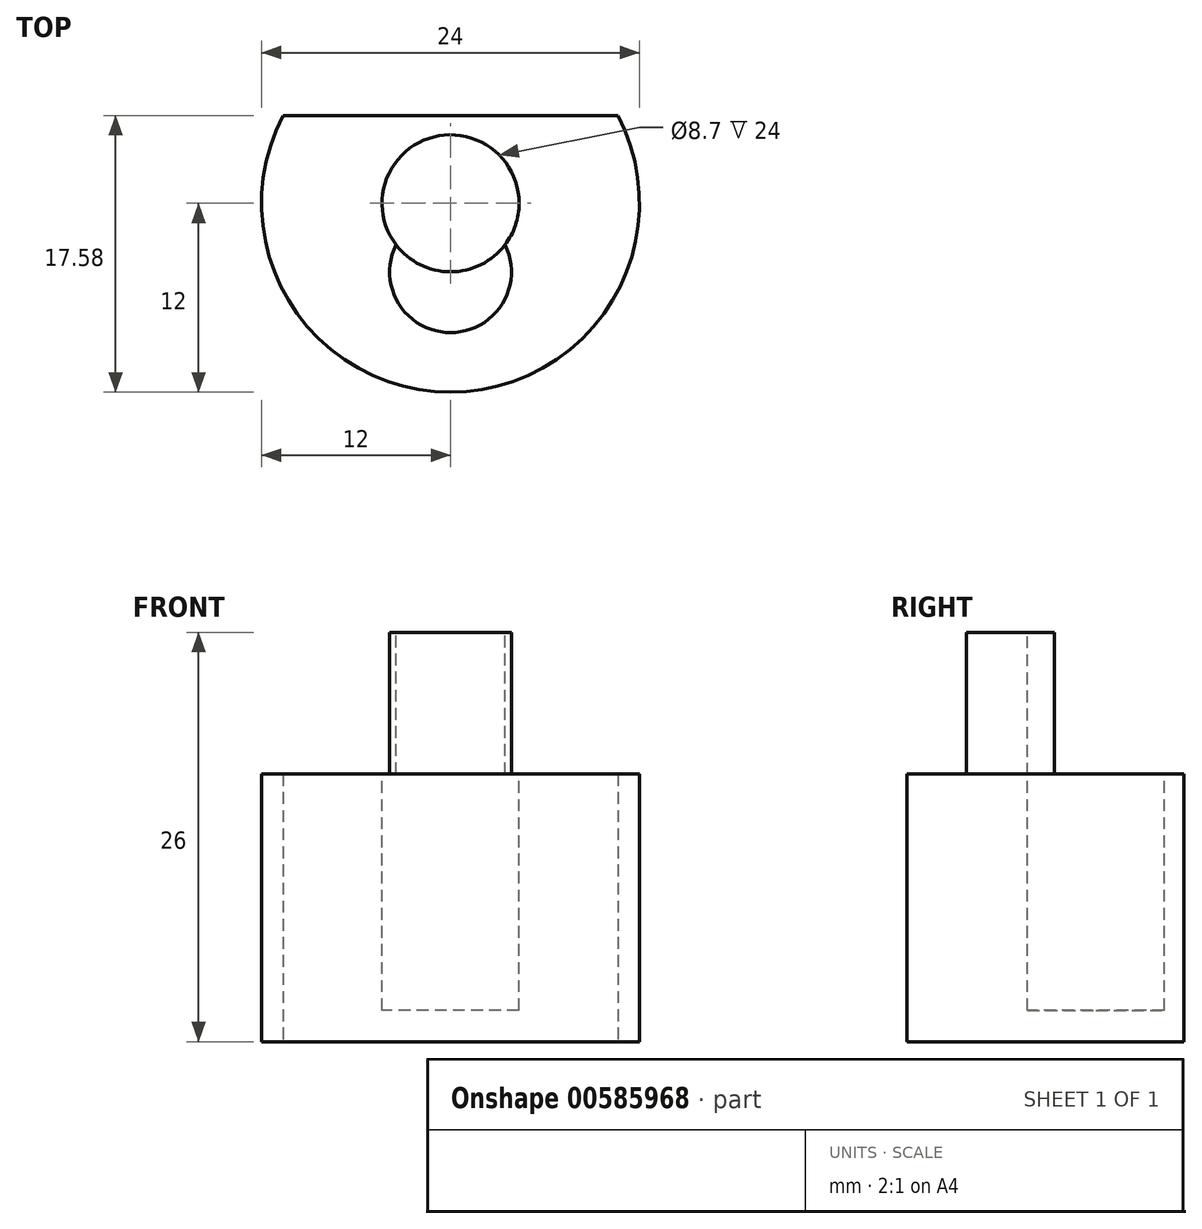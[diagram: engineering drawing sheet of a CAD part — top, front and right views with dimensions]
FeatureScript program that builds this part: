
annotation { "Feature Type Name" : "Feature", "Feature Type Description" : "" }
export const myFeature = defineFeature(function(context is Context, id is Id, definition is map)
    precondition{}
    {
        {
            var Q0;
            Q0=qCreatedBy(makeId("Top.planeOp"),FACE);
            var sketch = newSketch(context, id + "F0", { "sketchPlane" : qUnion([Q0])});
            skCircle(sketch, "E0", {"center": v(0, 0) * mm, "radius": 12 * mm});
            skSolve(sketch);
        }
        {
            var Q0;
            Q0 = qSketchRegion(id + "F0", true);
            extrude(context, id + "F1", {"entities" : qUnion([Q0]), "depth" : 26 * mm, "offsetDistance" : 25 * mm});
        }
        {
            var Q0;
            Q0=makeQuery(id+"F1.opExtrude","CAP_FACE",FACE,{"disambiguationData":[OSD([sQuery(id+"F0.wireOp",EDGE,"E0")])],"isStart":false});
            var sketch = newSketch(context, id + "F2", { "sketchPlane" : qUnion([Q0])});
            skCircle(sketch, "E1", {"center": v(0, 0) * mm, "radius": 4.35 * mm});
            skArc(sketch, "E2", {"start": v(-3.46, -2.63) * mm, "mid": v(0, -8.21) * mm, "end": v(3.46, -2.63) * mm});
            skSolve(sketch);
        }
        {
            var Q0;
            {var subQ0=sQuery(id+"F2.wireOp",EDGE,"E2");Q0=makeQuery(id+"F2.imprint","IMPRINT",FACE,{"disambiguationData":[TD([[makeQuery(id+"F2.imprint","IMPRINT",EDGE,{"derivedFrom":subQ0}),-1.0]])]});}
            var Q1;
            {var subQ0=sQuery(id+"F2.wireOp",EDGE,"E2");var subQ1=sQuery(id+"F2.wireOp",EDGE,"E1");var subQ2=makeQuery(id+"F2.imprint","INTERSECT",VERTEX,{"disambiguationData":[OD(0.0)],"derivedFrom":[subQ1,subQ0]});Q1=makeQuery(id+"F2.imprint","IMPRINT",FACE,{"disambiguationData":[TD([[makeQuery(id+"F2.imprint","IMPRINT",EDGE,{"disambiguationData":[TD([[subQ2,-1.0]])],"derivedFrom":subQ1}),1.0]])]});}
            extrude(context, id + "F3", {"entities" : qUnion([Q0, Q1]), "operationType" : NewBodyOperationType.REMOVE, "oppositeDirection" : true, "depth" : 9 * mm, "offsetDistance" : 25 * mm});
        }
        {
            var Q0;
            Q0=makeQuery(id+"F3.boolean.opBoolean","COPY",FACE,{"derivedFrom":makeQuery(id+"F3.opExtrude","CAP_FACE",FACE,{"disambiguationData":[OSD([sQuery(id+"F0.wireOp",EDGE,"E0"),sQuery(id+"F2.wireOp",EDGE,"E1"),sQuery(id+"F2.wireOp",EDGE,"E2")])],"isStart":false})});
            var sketch = newSketch(context, id + "F4", { "sketchPlane" : qUnion([Q0])});
            skCircle(sketch, "E3", {"center": v(0, 0) * mm, "radius": 4.35 * mm});
            skSolve(sketch);
        }
        {
            var Q0;
            {var subQ0=sQuery(id+"F4.wireOp",EDGE,"E3");var subQ1=makeQuery(id+"F3.boolean.opBoolean","COPY",EDGE,{"derivedFrom":makeQuery(id+"F3.opExtrude","CAP_EDGE",EDGE,{"disambiguationData":[OSD([sQuery(id+"F2.wireOp",EDGE,"E2")])],"isStart":false})});var subQ2=makeQuery(id+"F4.imprint","INTERSECT",VERTEX,{"disambiguationData":[OD(0.0)],"derivedFrom":[subQ1,subQ0]});Q0=makeQuery(id+"F4.imprint","IMPRINT",FACE,{"disambiguationData":[TD([[makeQuery(id+"F4.imprint","IMPRINT",EDGE,{"disambiguationData":[TD([[subQ2,-1.0]])],"derivedFrom":subQ0}),1.0]])]});}
            extrude(context, id + "F5", {"entities" : qUnion([Q0]), "operationType" : NewBodyOperationType.REMOVE, "oppositeDirection" : true, "depth" : 15 * mm, "offsetDistance" : 25 * mm});
        }
        {
            var Q0;
            Q0=qCreatedBy(makeId("Front.planeOp"),FACE);
            cPlane(context, id + "F6", {"entities" : qUnion([Q0]), "cplaneType" : CPlaneType.OFFSET, "offset" : 12 * mm, "oppositeDirection" : true, "width" : 150 * mm, "height" : 150 * mm});
        }
        {
            var Q0;
            Q0=qCreatedBy(id+"F6.planeOp",FACE);
            var sketch = newSketch(context, id + "F7", { "sketchPlane" : qUnion([Q0])});
            skLineSegment(sketch, "E4.bottom", {"start": v(0, 0) * mm, "end": v(-12, 0) * mm});
            skLineSegment(sketch, "E4.top", {"start": v(0, 17) * mm, "end": v(-12, 17) * mm});
            skLineSegment(sketch, "E4.left", {"start": v(0, 0) * mm, "end": v(0, 17) * mm});
            skLineSegment(sketch, "E4.right", {"start": v(-12, 0) * mm, "end": v(-12, 17) * mm});
            skLineSegment(sketch, "E5.bottom", {"start": v(0, 0) * mm, "end": v(12, 0) * mm});
            skLineSegment(sketch, "E5.top", {"start": v(0, 17) * mm, "end": v(12, 17) * mm});
            skLineSegment(sketch, "E5.right", {"start": v(12, 0) * mm, "end": v(12, 17) * mm});
            skSolve(sketch);
        }
        {
            var Q0;
            Q0=makeQuery(id+"F7.imprint","IMPRINT",FACE,{"disambiguationData":[TD([[makeQuery(id+"F7.imprint","IMPRINT",EDGE,{"derivedFrom":sQuery(id+"F7.wireOp",EDGE,"E5.bottom")}),1.0]])]});
            var Q1;
            Q1=makeQuery(id+"F7.imprint","IMPRINT",FACE,{"disambiguationData":[TD([[makeQuery(id+"F7.imprint","IMPRINT",EDGE,{"derivedFrom":sQuery(id+"F7.wireOp",EDGE,"E4.bottom")}),-1.0]])]});
            extrude(context, id + "F8", {"entities" : qUnion([Q0, Q1]), "operationType" : NewBodyOperationType.REMOVE, "depth" : 6.42 * mm, "offsetDistance" : 25 * mm});
        }
    });
